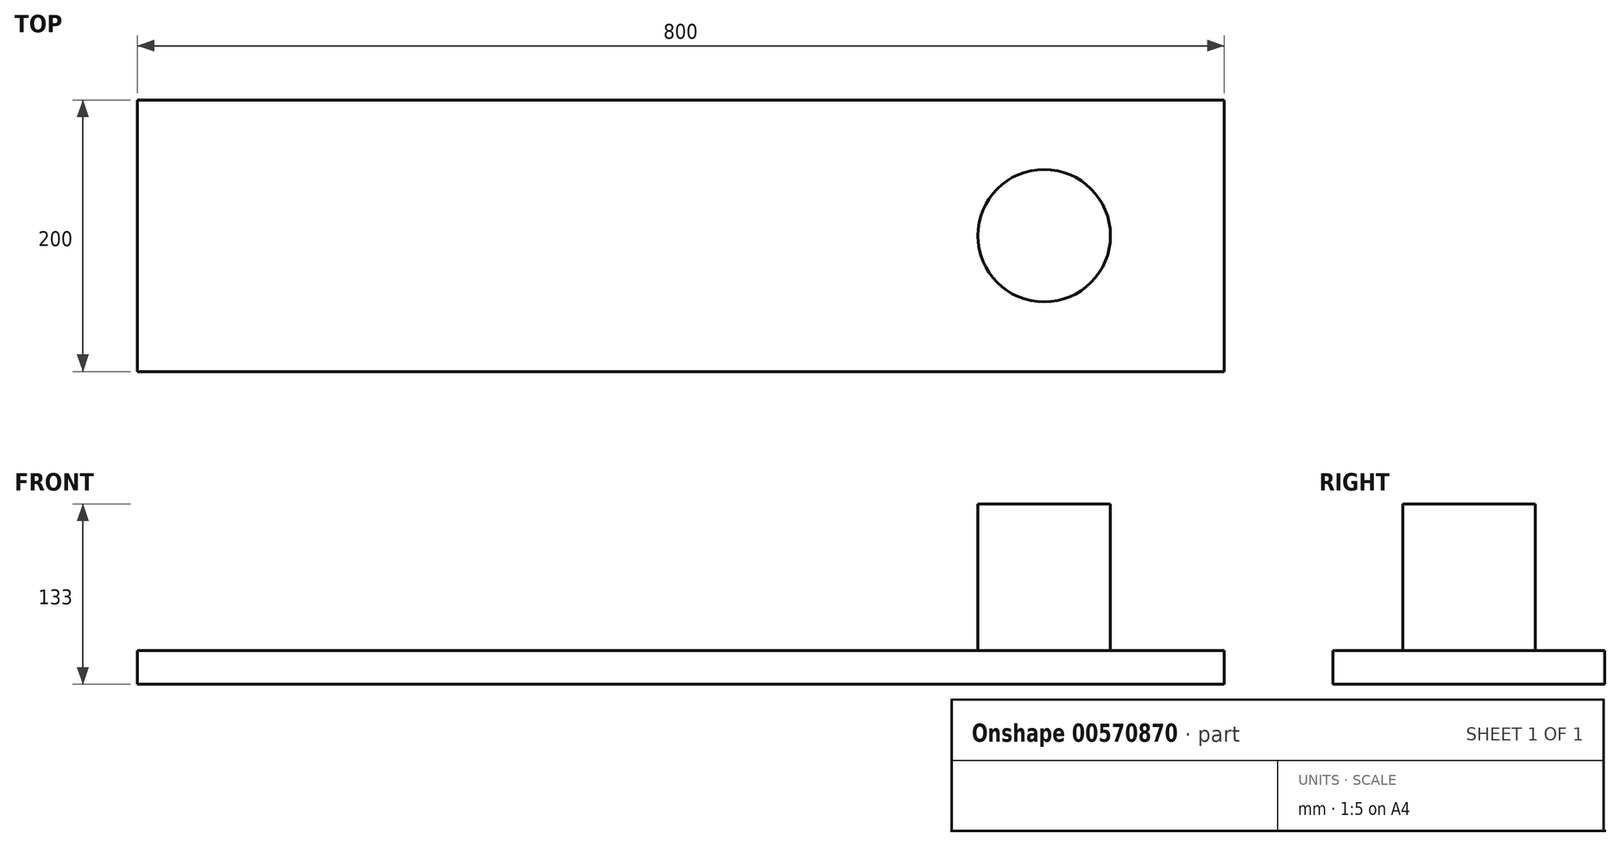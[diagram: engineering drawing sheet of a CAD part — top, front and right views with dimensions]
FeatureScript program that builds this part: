
annotation { "Feature Type Name" : "Feature", "Feature Type Description" : "" }
export const myFeature = defineFeature(function(context is Context, id is Id, definition is map)
    precondition{}
    {
        {
            var Q0;
            Q0=qCreatedBy(makeId("Top.planeOp"),FACE);
            var sketch = newSketch(context, id + "F0", { "sketchPlane" : qUnion([Q0])});
            skLineSegment(sketch, "E0.bottom", {"start": v(-400, 100) * mm, "end": v(400, 100) * mm});
            skLineSegment(sketch, "E0.top", {"start": v(-400, -100) * mm, "end": v(400, -100) * mm});
            skLineSegment(sketch, "E0.left", {"start": v(-400, 100) * mm, "end": v(-400, -100) * mm});
            skLineSegment(sketch, "E0.right", {"start": v(400, 100) * mm, "end": v(400, -100) * mm});
            skPoint(sketch, "E0.middle", {"position": v(0, 0) * mm});
            skSolve(sketch);
        }
        {
            var Q0;
            Q0=makeQuery(id+"F0.imprint","IMPRINT",FACE,{"disambiguationData":[TD([[makeQuery(id+"F0.imprint","IMPRINT",EDGE,{"derivedFrom":sQuery(id+"F0.wireOp",EDGE,"E0.bottom")}),-1.0]])]});
            extrude(context, id + "F1", {"entities" : qUnion([Q0]), "depth" : 25 * mm, "offsetDistance" : 25 * mm});
        }
        {
            var Q0;
            Q0=makeQuery(id+"F1.opExtrude","CAP_FACE",FACE,{"disambiguationData":[OSD([sQuery(id+"F0.wireOp",EDGE,"E0.bottom"),sQuery(id+"F0.wireOp",EDGE,"E0.top"),sQuery(id+"F0.wireOp",EDGE,"E0.left"),sQuery(id+"F0.wireOp",EDGE,"E0.right")])],"isStart":true});
            var sketch = newSketch(context, id + "F2", { "sketchPlane" : qUnion([Q0])});
            skCircle(sketch, "E1", {"center": v(267.43, 0) * mm, "radius": 48.8 * mm});
            skSolve(sketch);
        }
        {
            var Q0;
            Q0=makeQuery(id+"F2.imprint","IMPRINT",FACE,{"disambiguationData":[TD([[makeQuery(id+"F2.imprint","IMPRINT",EDGE,{"derivedFrom":sQuery(id+"F2.wireOp",EDGE,"E1")}),1.0]])]});
            extrude(context, id + "F3", {"entities" : qUnion([Q0]), "operationType" : NewBodyOperationType.ADD, "oppositeDirection" : true, "depth" : 133 * mm, "offsetDistance" : 25 * mm});
        }
    });
